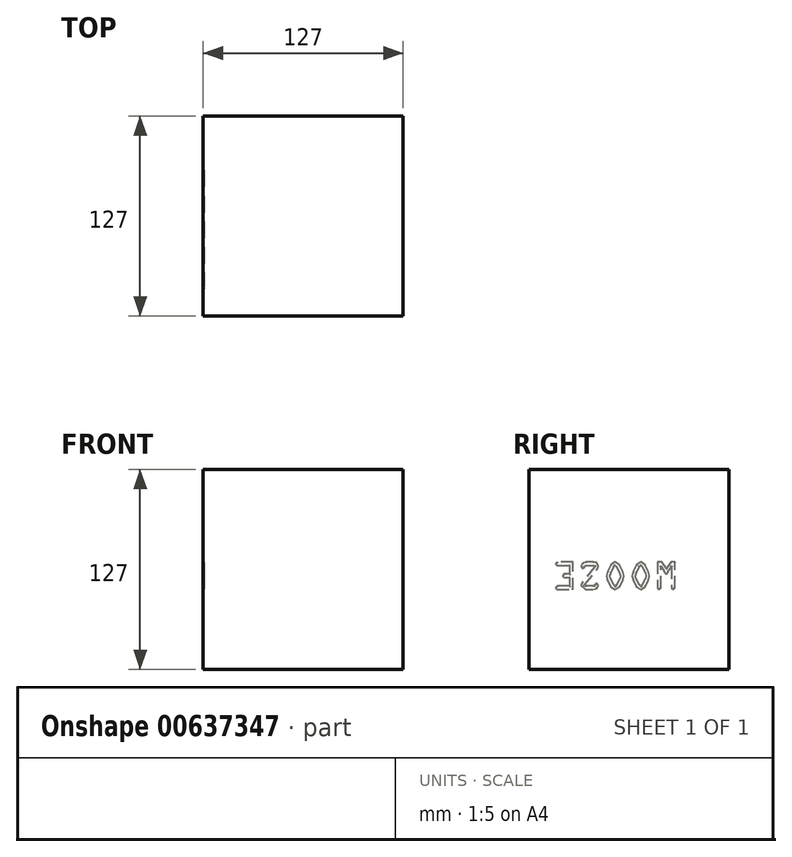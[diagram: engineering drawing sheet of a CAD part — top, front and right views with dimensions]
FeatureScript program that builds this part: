
annotation { "Feature Type Name" : "Feature", "Feature Type Description" : "" }
export const myFeature = defineFeature(function(context is Context, id is Id, definition is map)
    precondition{}
    {
        {
            var Q0;
            Q0=qCreatedBy(makeId("Top.planeOp"),FACE);
            var sketch = newSketch(context, id + "F0", { "sketchPlane" : qUnion([Q0])});
            skLineSegment(sketch, "E0.bottom", {"start": v(0, 0) * mm, "end": v(127, 0) * mm});
            skLineSegment(sketch, "E0.top", {"start": v(0, -127) * mm, "end": v(127, -127) * mm});
            skLineSegment(sketch, "E0.left", {"start": v(0, 0) * mm, "end": v(0, -127) * mm});
            skLineSegment(sketch, "E0.right", {"start": v(127, 0) * mm, "end": v(127, -127) * mm});
            skSolve(sketch);
        }
        {
            var Q0;
            Q0 = qSketchRegion(id + "F0", true);
            extrude(context, id + "F1", {"entities" : qUnion([Q0]), "depth" : 127 * mm, "offsetDistance" : 25.4 * mm});
        }
        {
            var Q0;
            Q0=makeQuery(id+"F1.opExtrude","SWEPT_FACE",FACE,{"disambiguationData":[OSD([sQuery(id+"F0.wireOp",EDGE,"E0.left")])]});
            var sketch = newSketch(context, id + "F2", { "sketchPlane" : qUnion([Q0])});
            skLineSegment(sketch, "E1", {"start": v(42.6, 68.23) * mm, "end": v(45.42, 68.23) * mm});
            skLineSegment(sketch, "E2", {"start": v(45.42, 68.23) * mm, "end": v(45.42, 51.8) * mm});
            skLineSegment(sketch, "E3", {"start": v(45.42, 51.8) * mm, "end": v(44.29, 50.67) * mm});
            skLineSegment(sketch, "E4", {"start": v(44.29, 50.67) * mm, "end": v(43.16, 51.8) * mm});
            skLineSegment(sketch, "E5", {"start": v(43.16, 51.8) * mm, "end": v(43.16, 65.12) * mm});
            skLineSegment(sketch, "E6", {"start": v(43.16, 65.12) * mm, "end": v(43.11, 65.12) * mm});
            skLineSegment(sketch, "E7", {"start": v(43.11, 65.12) * mm, "end": v(40.97, 61.93) * mm});
            skLineSegment(sketch, "E8", {"start": v(40.97, 61.93) * mm, "end": v(40.97, 61.57) * mm});
            skLineSegment(sketch, "E9", {"start": v(40.97, 61.57) * mm, "end": v(39.84, 60.22) * mm});
            skLineSegment(sketch, "E10", {"start": v(39.84, 60.22) * mm, "end": v(38.7, 61.57) * mm});
            skLineSegment(sketch, "E11", {"start": v(38.7, 61.57) * mm, "end": v(38.7, 61.93) * mm});
            skLineSegment(sketch, "E12", {"start": v(38.7, 61.93) * mm, "end": v(36.57, 65.12) * mm});
            skLineSegment(sketch, "E13", {"start": v(36.57, 65.12) * mm, "end": v(36.52, 65.12) * mm});
            skLineSegment(sketch, "E14", {"start": v(36.52, 65.12) * mm, "end": v(36.52, 51.8) * mm});
            skLineSegment(sketch, "E15", {"start": v(36.52, 51.8) * mm, "end": v(35.4, 50.67) * mm});
            skLineSegment(sketch, "E16", {"start": v(35.4, 50.67) * mm, "end": v(34.26, 51.8) * mm});
            skLineSegment(sketch, "E17", {"start": v(34.26, 51.8) * mm, "end": v(34.26, 68.23) * mm});
            skLineSegment(sketch, "E18", {"start": v(34.26, 68.23) * mm, "end": v(37.08, 68.23) * mm});
            skLineSegment(sketch, "E19", {"start": v(37.08, 68.23) * mm, "end": v(39.84, 64.26) * mm});
            skLineSegment(sketch, "E20", {"start": v(39.84, 64.26) * mm, "end": v(42.6, 68.23) * mm});
            skLineSegment(sketch, "E21", {"start": v(61.08, 61.89) * mm, "end": v(61.67, 59.38) * mm});
            skLineSegment(sketch, "E22", {"start": v(61.67, 59.38) * mm, "end": v(60.93, 56.7) * mm});
            skLineSegment(sketch, "E23", {"start": v(60.93, 56.7) * mm, "end": v(58.85, 52.54) * mm});
            skLineSegment(sketch, "E24", {"start": v(58.85, 52.54) * mm, "end": v(56.1, 50.67) * mm});
            skLineSegment(sketch, "E25", {"start": v(56.1, 50.67) * mm, "end": v(53.34, 52.54) * mm});
            skLineSegment(sketch, "E26", {"start": v(53.34, 52.54) * mm, "end": v(51.26, 56.7) * mm});
            skLineSegment(sketch, "E27", {"start": v(51.26, 56.7) * mm, "end": v(50.52, 59.38) * mm});
            skLineSegment(sketch, "E28", {"start": v(50.52, 59.38) * mm, "end": v(51.1, 61.89) * mm});
            skLineSegment(sketch, "E29", {"start": v(51.1, 61.89) * mm, "end": v(53.36, 66.38) * mm});
            skLineSegment(sketch, "E30", {"start": v(53.36, 66.38) * mm, "end": v(56.1, 68.23) * mm});
            skLineSegment(sketch, "E31", {"start": v(56.1, 68.23) * mm, "end": v(58.83, 66.38) * mm});
            skLineSegment(sketch, "E32", {"start": v(58.83, 66.38) * mm, "end": v(61.08, 61.89) * mm});
            skLineSegment(sketch, "E33", {"start": v(56.86, 65.3) * mm, "end": v(56.1, 65.97) * mm});
            skLineSegment(sketch, "E34", {"start": v(56.1, 65.97) * mm, "end": v(55.33, 65.3) * mm});
            skLineSegment(sketch, "E35", {"start": v(55.33, 65.3) * mm, "end": v(53.3, 61.21) * mm});
            skLineSegment(sketch, "E36", {"start": v(53.3, 61.21) * mm, "end": v(52.78, 59.38) * mm});
            skLineSegment(sketch, "E37", {"start": v(52.78, 59.38) * mm, "end": v(53.16, 57.9) * mm});
            skLineSegment(sketch, "E38", {"start": v(53.16, 57.9) * mm, "end": v(55.33, 53.6) * mm});
            skLineSegment(sketch, "E39", {"start": v(55.33, 53.6) * mm, "end": v(56.1, 52.93) * mm});
            skLineSegment(sketch, "E40", {"start": v(56.1, 52.93) * mm, "end": v(56.86, 53.6) * mm});
            skLineSegment(sketch, "E41", {"start": v(56.86, 53.6) * mm, "end": v(59.03, 57.9) * mm});
            skLineSegment(sketch, "E42", {"start": v(59.03, 57.9) * mm, "end": v(59.41, 59.38) * mm});
            skLineSegment(sketch, "E43", {"start": v(59.41, 59.38) * mm, "end": v(58.9, 61.21) * mm});
            skLineSegment(sketch, "E44", {"start": v(58.9, 61.21) * mm, "end": v(56.86, 65.3) * mm});
            skLineSegment(sketch, "E45", {"start": v(77.34, 61.89) * mm, "end": v(77.93, 59.38) * mm});
            skLineSegment(sketch, "E46", {"start": v(77.93, 59.38) * mm, "end": v(77.18, 56.7) * mm});
            skLineSegment(sketch, "E47", {"start": v(77.18, 56.7) * mm, "end": v(75.1, 52.54) * mm});
            skLineSegment(sketch, "E48", {"start": v(75.1, 52.54) * mm, "end": v(72.35, 50.67) * mm});
            skLineSegment(sketch, "E49", {"start": v(72.35, 50.67) * mm, "end": v(69.6, 52.54) * mm});
            skLineSegment(sketch, "E50", {"start": v(69.6, 52.54) * mm, "end": v(67.52, 56.7) * mm});
            skLineSegment(sketch, "E51", {"start": v(67.52, 56.7) * mm, "end": v(66.77, 59.38) * mm});
            skLineSegment(sketch, "E52", {"start": v(66.77, 59.38) * mm, "end": v(67.36, 61.89) * mm});
            skLineSegment(sketch, "E53", {"start": v(67.36, 61.89) * mm, "end": v(69.62, 66.38) * mm});
            skLineSegment(sketch, "E54", {"start": v(69.62, 66.38) * mm, "end": v(72.35, 68.23) * mm});
            skLineSegment(sketch, "E55", {"start": v(72.35, 68.23) * mm, "end": v(75.08, 66.38) * mm});
            skLineSegment(sketch, "E56", {"start": v(75.08, 66.38) * mm, "end": v(77.34, 61.89) * mm});
            skLineSegment(sketch, "E57", {"start": v(73.12, 65.3) * mm, "end": v(72.35, 65.97) * mm});
            skLineSegment(sketch, "E58", {"start": v(72.35, 65.97) * mm, "end": v(71.58, 65.3) * mm});
            skLineSegment(sketch, "E59", {"start": v(71.58, 65.3) * mm, "end": v(69.55, 61.21) * mm});
            skLineSegment(sketch, "E60", {"start": v(69.55, 61.21) * mm, "end": v(69.03, 59.38) * mm});
            skLineSegment(sketch, "E61", {"start": v(69.03, 59.38) * mm, "end": v(69.42, 57.9) * mm});
            skLineSegment(sketch, "E62", {"start": v(69.42, 57.9) * mm, "end": v(71.58, 53.6) * mm});
            skLineSegment(sketch, "E63", {"start": v(71.58, 53.6) * mm, "end": v(72.35, 52.93) * mm});
            skLineSegment(sketch, "E64", {"start": v(72.35, 52.93) * mm, "end": v(73.12, 53.6) * mm});
            skLineSegment(sketch, "E65", {"start": v(73.12, 53.6) * mm, "end": v(75.29, 57.9) * mm});
            skLineSegment(sketch, "E66", {"start": v(75.29, 57.9) * mm, "end": v(75.67, 59.38) * mm});
            skLineSegment(sketch, "E67", {"start": v(75.67, 59.38) * mm, "end": v(75.15, 61.21) * mm});
            skLineSegment(sketch, "E68", {"start": v(75.15, 61.21) * mm, "end": v(73.12, 65.3) * mm});
            skLineSegment(sketch, "E69", {"start": v(93.4, 55.1) * mm, "end": v(94.18, 53.22) * mm});
            skLineSegment(sketch, "E70", {"start": v(94.18, 53.22) * mm, "end": v(91.34, 50.67) * mm});
            skLineSegment(sketch, "E71", {"start": v(91.34, 50.67) * mm, "end": v(86.37, 50.67) * mm});
            skLineSegment(sketch, "E72", {"start": v(86.37, 50.67) * mm, "end": v(84.1, 51.39) * mm});
            skLineSegment(sketch, "E73", {"start": v(84.1, 51.39) * mm, "end": v(83.03, 53.49) * mm});
            skLineSegment(sketch, "E74", {"start": v(83.03, 53.49) * mm, "end": v(84.23, 54.84) * mm});
            skLineSegment(sketch, "E75", {"start": v(84.23, 54.84) * mm, "end": v(85.29, 53.7) * mm});
            skLineSegment(sketch, "E76", {"start": v(85.29, 53.7) * mm, "end": v(86.28, 52.93) * mm});
            skLineSegment(sketch, "E77", {"start": v(86.28, 52.93) * mm, "end": v(91.18, 52.93) * mm});
            skLineSegment(sketch, "E78", {"start": v(91.18, 52.93) * mm, "end": v(91.92, 53.2) * mm});
            skLineSegment(sketch, "E79", {"start": v(91.92, 53.2) * mm, "end": v(91.52, 53.85) * mm});
            skLineSegment(sketch, "E80", {"start": v(91.52, 53.85) * mm, "end": v(83.77, 63.8) * mm});
            skLineSegment(sketch, "E81", {"start": v(83.77, 63.8) * mm, "end": v(83.03, 65.66) * mm});
            skLineSegment(sketch, "E82", {"start": v(83.03, 65.66) * mm, "end": v(84.23, 67.83) * mm});
            skLineSegment(sketch, "E83", {"start": v(84.23, 67.83) * mm, "end": v(86.1, 68.23) * mm});
            skLineSegment(sketch, "E84", {"start": v(86.1, 68.23) * mm, "end": v(90.89, 68.23) * mm});
            skLineSegment(sketch, "E85", {"start": v(90.89, 68.23) * mm, "end": v(93.12, 67.49) * mm});
            skLineSegment(sketch, "E86", {"start": v(93.12, 67.49) * mm, "end": v(94.18, 65.34) * mm});
            skLineSegment(sketch, "E87", {"start": v(94.18, 65.34) * mm, "end": v(93, 64.03) * mm});
            skLineSegment(sketch, "E88", {"start": v(93, 64.03) * mm, "end": v(91.92, 65.1) * mm});
            skLineSegment(sketch, "E89", {"start": v(91.92, 65.1) * mm, "end": v(90.84, 65.97) * mm});
            skLineSegment(sketch, "E90", {"start": v(90.84, 65.97) * mm, "end": v(86.05, 65.97) * mm});
            skLineSegment(sketch, "E91", {"start": v(86.05, 65.97) * mm, "end": v(85.29, 65.66) * mm});
            skLineSegment(sketch, "E92", {"start": v(85.29, 65.66) * mm, "end": v(85.63, 65.05) * mm});
            skLineSegment(sketch, "E93", {"start": v(85.63, 65.05) * mm, "end": v(93.4, 55.1) * mm});
            skLineSegment(sketch, "E94", {"start": v(109.3, 52.93) * mm, "end": v(110.44, 51.8) * mm});
            skLineSegment(sketch, "E95", {"start": v(110.44, 51.8) * mm, "end": v(109.3, 50.67) * mm});
            skLineSegment(sketch, "E96", {"start": v(109.3, 50.67) * mm, "end": v(99.29, 50.67) * mm});
            skLineSegment(sketch, "E97", {"start": v(99.29, 50.67) * mm, "end": v(99.29, 68.23) * mm});
            skLineSegment(sketch, "E98", {"start": v(99.29, 68.23) * mm, "end": v(109.3, 68.23) * mm});
            skLineSegment(sketch, "E99", {"start": v(109.3, 68.23) * mm, "end": v(110.44, 67.1) * mm});
            skLineSegment(sketch, "E100", {"start": v(110.44, 67.1) * mm, "end": v(109.3, 65.97) * mm});
            skLineSegment(sketch, "E101", {"start": v(109.3, 65.97) * mm, "end": v(101.54, 65.97) * mm});
            skLineSegment(sketch, "E102", {"start": v(101.54, 65.97) * mm, "end": v(101.54, 60.58) * mm});
            skLineSegment(sketch, "E103", {"start": v(101.54, 60.58) * mm, "end": v(104.86, 60.58) * mm});
            skLineSegment(sketch, "E104", {"start": v(104.86, 60.58) * mm, "end": v(106, 59.45) * mm});
            skLineSegment(sketch, "E105", {"start": v(106, 59.45) * mm, "end": v(104.86, 58.32) * mm});
            skLineSegment(sketch, "E106", {"start": v(104.86, 58.32) * mm, "end": v(101.54, 58.32) * mm});
            skLineSegment(sketch, "E107", {"start": v(101.54, 58.32) * mm, "end": v(101.54, 52.93) * mm});
            skLineSegment(sketch, "E108", {"start": v(101.54, 52.93) * mm, "end": v(109.3, 52.93) * mm});
            skSolve(sketch);
        }
        {
            var Q0;
            Q0 = qSketchRegion(id + "F2", true);
            extrude(context, id + "F3", {"entities" : qUnion([Q0]), "operationType" : NewBodyOperationType.REMOVE, "oppositeDirection" : true, "depth" : 0.5 * mm, "offsetDistance" : 25.4 * mm});
        }
        {
            var Q0;
            Q0=makeQuery(id+"F3.boolean.opBoolean","COPY",FACE,{"derivedFrom":makeQuery(id+"F3.opExtrude","CAP_FACE",FACE,{"disambiguationData":[OSD([sQuery(id+"F2.wireOp",EDGE,"E1"),sQuery(id+"F2.wireOp",EDGE,"E2"),sQuery(id+"F2.wireOp",EDGE,"E3"),sQuery(id+"F2.wireOp",EDGE,"E4"),sQuery(id+"F2.wireOp",EDGE,"E5"),sQuery(id+"F2.wireOp",EDGE,"E6"),sQuery(id+"F2.wireOp",EDGE,"E7"),sQuery(id+"F2.wireOp",EDGE,"E8"),sQuery(id+"F2.wireOp",EDGE,"E9"),sQuery(id+"F2.wireOp",EDGE,"E10"),sQuery(id+"F2.wireOp",EDGE,"E11"),sQuery(id+"F2.wireOp",EDGE,"E12"),sQuery(id+"F2.wireOp",EDGE,"E13"),sQuery(id+"F2.wireOp",EDGE,"E14"),sQuery(id+"F2.wireOp",EDGE,"E15"),sQuery(id+"F2.wireOp",EDGE,"E16"),sQuery(id+"F2.wireOp",EDGE,"E17"),sQuery(id+"F2.wireOp",EDGE,"E18"),sQuery(id+"F2.wireOp",EDGE,"E19"),sQuery(id+"F2.wireOp",EDGE,"E20")])],"isStart":false})});
            var Q1;
            Q1=makeQuery(id+"F3.boolean.opBoolean","COPY",FACE,{"derivedFrom":makeQuery(id+"F3.opExtrude","CAP_FACE",FACE,{"disambiguationData":[OSD([sQuery(id+"F2.wireOp",EDGE,"E21"),sQuery(id+"F2.wireOp",EDGE,"E22"),sQuery(id+"F2.wireOp",EDGE,"E23"),sQuery(id+"F2.wireOp",EDGE,"E24"),sQuery(id+"F2.wireOp",EDGE,"E25"),sQuery(id+"F2.wireOp",EDGE,"E26"),sQuery(id+"F2.wireOp",EDGE,"E27"),sQuery(id+"F2.wireOp",EDGE,"E28"),sQuery(id+"F2.wireOp",EDGE,"E29"),sQuery(id+"F2.wireOp",EDGE,"E30"),sQuery(id+"F2.wireOp",EDGE,"E31"),sQuery(id+"F2.wireOp",EDGE,"E32"),sQuery(id+"F2.wireOp",EDGE,"E33"),sQuery(id+"F2.wireOp",EDGE,"E34"),sQuery(id+"F2.wireOp",EDGE,"E35"),sQuery(id+"F2.wireOp",EDGE,"E36"),sQuery(id+"F2.wireOp",EDGE,"E37"),sQuery(id+"F2.wireOp",EDGE,"E38"),sQuery(id+"F2.wireOp",EDGE,"E39"),sQuery(id+"F2.wireOp",EDGE,"E40"),sQuery(id+"F2.wireOp",EDGE,"E41"),sQuery(id+"F2.wireOp",EDGE,"E42"),sQuery(id+"F2.wireOp",EDGE,"E43"),sQuery(id+"F2.wireOp",EDGE,"E44")])],"isStart":false})});
            var Q2;
            Q2=makeQuery(id+"F3.boolean.opBoolean","COPY",FACE,{"derivedFrom":makeQuery(id+"F3.opExtrude","CAP_FACE",FACE,{"disambiguationData":[OSD([sQuery(id+"F2.wireOp",EDGE,"E45"),sQuery(id+"F2.wireOp",EDGE,"E46"),sQuery(id+"F2.wireOp",EDGE,"E47"),sQuery(id+"F2.wireOp",EDGE,"E48"),sQuery(id+"F2.wireOp",EDGE,"E49"),sQuery(id+"F2.wireOp",EDGE,"E50"),sQuery(id+"F2.wireOp",EDGE,"E51"),sQuery(id+"F2.wireOp",EDGE,"E52"),sQuery(id+"F2.wireOp",EDGE,"E53"),sQuery(id+"F2.wireOp",EDGE,"E54"),sQuery(id+"F2.wireOp",EDGE,"E55"),sQuery(id+"F2.wireOp",EDGE,"E56"),sQuery(id+"F2.wireOp",EDGE,"E57"),sQuery(id+"F2.wireOp",EDGE,"E58"),sQuery(id+"F2.wireOp",EDGE,"E59"),sQuery(id+"F2.wireOp",EDGE,"E60"),sQuery(id+"F2.wireOp",EDGE,"E61"),sQuery(id+"F2.wireOp",EDGE,"E62"),sQuery(id+"F2.wireOp",EDGE,"E63"),sQuery(id+"F2.wireOp",EDGE,"E64"),sQuery(id+"F2.wireOp",EDGE,"E65"),sQuery(id+"F2.wireOp",EDGE,"E66"),sQuery(id+"F2.wireOp",EDGE,"E67"),sQuery(id+"F2.wireOp",EDGE,"E68")])],"isStart":false})});
            var Q3;
            Q3=makeQuery(id+"F3.boolean.opBoolean","COPY",FACE,{"derivedFrom":makeQuery(id+"F3.opExtrude","CAP_FACE",FACE,{"disambiguationData":[OSD([sQuery(id+"F2.wireOp",EDGE,"E69"),sQuery(id+"F2.wireOp",EDGE,"E70"),sQuery(id+"F2.wireOp",EDGE,"E71"),sQuery(id+"F2.wireOp",EDGE,"E72"),sQuery(id+"F2.wireOp",EDGE,"E73"),sQuery(id+"F2.wireOp",EDGE,"E74"),sQuery(id+"F2.wireOp",EDGE,"E75"),sQuery(id+"F2.wireOp",EDGE,"E76"),sQuery(id+"F2.wireOp",EDGE,"E77"),sQuery(id+"F2.wireOp",EDGE,"E78"),sQuery(id+"F2.wireOp",EDGE,"E79"),sQuery(id+"F2.wireOp",EDGE,"E80"),sQuery(id+"F2.wireOp",EDGE,"E81"),sQuery(id+"F2.wireOp",EDGE,"E82"),sQuery(id+"F2.wireOp",EDGE,"E83"),sQuery(id+"F2.wireOp",EDGE,"E84"),sQuery(id+"F2.wireOp",EDGE,"E85"),sQuery(id+"F2.wireOp",EDGE,"E86"),sQuery(id+"F2.wireOp",EDGE,"E87"),sQuery(id+"F2.wireOp",EDGE,"E88"),sQuery(id+"F2.wireOp",EDGE,"E89"),sQuery(id+"F2.wireOp",EDGE,"E90"),sQuery(id+"F2.wireOp",EDGE,"E91"),sQuery(id+"F2.wireOp",EDGE,"E92"),sQuery(id+"F2.wireOp",EDGE,"E93")])],"isStart":false})});
            var Q4;
            Q4=makeQuery(id+"F3.boolean.opBoolean","COPY",FACE,{"derivedFrom":makeQuery(id+"F3.opExtrude","CAP_FACE",FACE,{"disambiguationData":[OSD([sQuery(id+"F2.wireOp",EDGE,"E94"),sQuery(id+"F2.wireOp",EDGE,"E95"),sQuery(id+"F2.wireOp",EDGE,"E96"),sQuery(id+"F2.wireOp",EDGE,"E97"),sQuery(id+"F2.wireOp",EDGE,"E98"),sQuery(id+"F2.wireOp",EDGE,"E99"),sQuery(id+"F2.wireOp",EDGE,"E100"),sQuery(id+"F2.wireOp",EDGE,"E101"),sQuery(id+"F2.wireOp",EDGE,"E102"),sQuery(id+"F2.wireOp",EDGE,"E103"),sQuery(id+"F2.wireOp",EDGE,"E104"),sQuery(id+"F2.wireOp",EDGE,"E105"),sQuery(id+"F2.wireOp",EDGE,"E106"),sQuery(id+"F2.wireOp",EDGE,"E107"),sQuery(id+"F2.wireOp",EDGE,"E108")])],"isStart":false})});
            fillet(context, id + "F4", {"entities" : qUnion([Q0, Q1, Q2, Q3, Q4]), "radius" : 0.5 * mm, "tangentPropagation" : true, "allowEdgeOverflow" : false});
        }
    });
